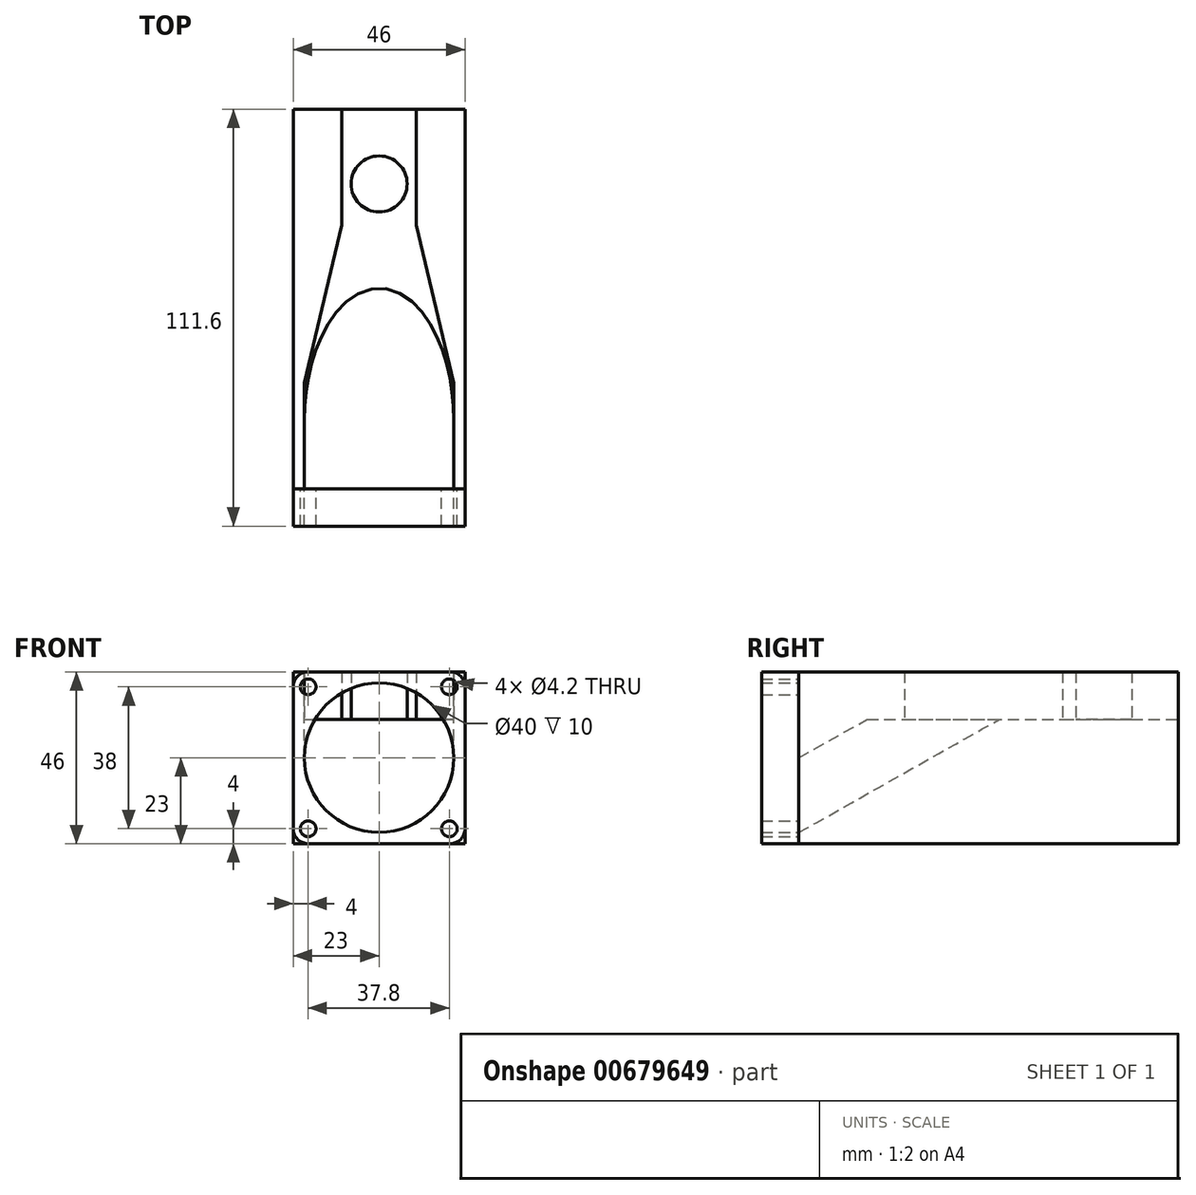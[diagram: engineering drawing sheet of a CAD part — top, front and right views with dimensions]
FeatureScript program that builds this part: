
annotation { "Feature Type Name" : "Feature", "Feature Type Description" : "" }
export const myFeature = defineFeature(function(context is Context, id is Id, definition is map)
    precondition{}
    {
        {
            var Q0;
            Q0=qCreatedBy(makeId("Front.planeOp"),FACE);
            var sketch = newSketch(context, id + "F0", { "sketchPlane" : qUnion([Q0])});
            skLineSegment(sketch, "E0.bottom", {"start": v(23, -23) * mm, "end": v(-23, -23) * mm});
            skLineSegment(sketch, "E0.top", {"start": v(23, 23) * mm, "end": v(-23, 23) * mm});
            skLineSegment(sketch, "E0.left", {"start": v(23, -23) * mm, "end": v(23, 23) * mm});
            skLineSegment(sketch, "E0.right", {"start": v(-23, -23) * mm, "end": v(-23, 23) * mm});
            skPoint(sketch, "E0.middle", {"position": v(0, 0) * mm});
            skSolve(sketch);
        }
        {
            var Q0;
            Q0=makeQuery(id+"F0.imprint","IMPRINT",FACE,{"disambiguationData":[TD([[makeQuery(id+"F0.imprint","IMPRINT",EDGE,{"derivedFrom":sQuery(id+"F0.wireOp",EDGE,"E0.bottom")}),-1.0]])]});
            extrude(context, id + "F1", {"entities" : qUnion([Q0]), "oppositeDirection" : true, "depth" : 101.6 * mm, "offsetDistance" : 25.4 * mm});
        }
        {
            var Q0;
            Q0=makeQuery(id+"F1.opExtrude","CAP_FACE",FACE,{"disambiguationData":[OSD([sQuery(id+"F0.wireOp",EDGE,"E0.bottom"),sQuery(id+"F0.wireOp",EDGE,"E0.top"),sQuery(id+"F0.wireOp",EDGE,"E0.left"),sQuery(id+"F0.wireOp",EDGE,"E0.right")])],"isStart":true});
            var sketch = newSketch(context, id + "F2", { "sketchPlane" : qUnion([Q0])});
            skArc(sketch, "E1", {"start": v(-20, 0) * mm, "mid": v(0, -20) * mm, "end": v(20, 0) * mm});
            skLineSegment(sketch, "E2.top", {"start": v(-20, 23) * mm, "end": v(20, 23) * mm});
            skLineSegment(sketch, "E2.left", {"start": v(-20, 0) * mm, "end": v(-20, 23) * mm});
            skLineSegment(sketch, "E2.right", {"start": v(20, 0) * mm, "end": v(20, 23) * mm});
            skSolve(sketch);
        }
        {
            var Q0;
            Q0=qCreatedBy(makeId("Right.planeOp"),FACE);
            var sketch = newSketch(context, id + "F3", { "sketchPlane" : qUnion([Q0])});
            skLineSegment(sketch, "E3", {"start": v(0, -20) * mm, "end": v(76.2, 23) * mm});
            skSolve(sketch);
        }
        {
            var Q0;
            Q0 = qSketchRegion(id + "F2", true);
            var Q1;
            Q1=sQuery(id+"F3.wireOp",EDGE,"E3");
            sweep(context, id + "F4", {"operationType" : NewBodyOperationType.REMOVE, "profiles" : qUnion([Q0]), "path" : qUnion([Q1])});
        }
        {
            var Q0;
            Q0=makeQuery(id+"F1.opExtrude","SWEPT_FACE",FACE,{"disambiguationData":[OSD([sQuery(id+"F0.wireOp",EDGE,"E0.top")])]});
            var sketch = newSketch(context, id + "F5", { "sketchPlane" : qUnion([Q0])});
            skLineSegment(sketch, "E4.bottom", {"start": v(-20, 0) * mm, "end": v(20, 0) * mm});
            skLineSegment(sketch, "E4.top", {"start": v(-20, 101.6) * mm, "end": v(20, 101.6) * mm});
            skLineSegment(sketch, "E4.left", {"start": v(-20, 0) * mm, "end": v(-20, 101.6) * mm});
            skLineSegment(sketch, "E4.right", {"start": v(20, 0) * mm, "end": v(20, 101.6) * mm});
            skSolve(sketch);
        }
        {
            var Q0;
            Q0 = qSketchRegion(id + "F5", true);
            extrude(context, id + "F6", {"entities" : qUnion([Q0]), "operationType" : NewBodyOperationType.REMOVE, "oppositeDirection" : true, "depth" : 12.7 * mm, "offsetDistance" : 25.4 * mm});
        }
        {
            var Q0;
            Q0=makeQuery(id+"F1.opExtrude","CAP_FACE",FACE,{"disambiguationData":[OSD([sQuery(id+"F0.wireOp",EDGE,"E0.bottom"),sQuery(id+"F0.wireOp",EDGE,"E0.top"),sQuery(id+"F0.wireOp",EDGE,"E0.left"),sQuery(id+"F0.wireOp",EDGE,"E0.right")])],"isStart":true});
            var sketch = newSketch(context, id + "F7", { "sketchPlane" : qUnion([Q0])});
            skCircle(sketch, "E5", {"center": v(0, 0) * mm, "radius": 20 * mm});
            skLineSegment(sketch, "E6.bottom", {"start": v(-23, -23) * mm, "end": v(23, -23) * mm});
            skLineSegment(sketch, "E6.top", {"start": v(-23, 23) * mm, "end": v(23, 23) * mm});
            skLineSegment(sketch, "E6.left", {"start": v(-23, -23) * mm, "end": v(-23, 23) * mm});
            skLineSegment(sketch, "E6.right", {"start": v(23, -23) * mm, "end": v(23, 23) * mm});
            skCircle(sketch, "E7", {"center": v(-19, 19) * mm, "radius": 2.1 * mm});
            skCircle(sketch, "E8", {"center": v(-19, -19) * mm, "radius": 2.1 * mm});
            skCircle(sketch, "E9", {"center": v(18.8, -19) * mm, "radius": 2.1 * mm});
            skCircle(sketch, "E10", {"center": v(18.8, 19) * mm, "radius": 2.1 * mm});
            skSolve(sketch);
        }
        {
            var Q0;
            Q0 = qSketchRegion(id + "F7", true);
            extrude(context, id + "F8", {"entities" : qUnion([Q0]), "depth" : 10 * mm, "offsetDistance" : 25.4 * mm});
        }
        {
            var Q0;
            Q0=makeQuery(id+"F8.opExtrude","SWEPT_EDGE",EDGE,{"disambiguationData":[OSD([sQuery(id+"F7.wireOp",EDGE,"E6.top"),sQuery(id+"F7.wireOp",EDGE,"E6.right")])]});
            var Q1;
            Q1=makeQuery(id+"F8.opExtrude","SWEPT_EDGE",EDGE,{"disambiguationData":[OSD([sQuery(id+"F7.wireOp",EDGE,"E6.top"),sQuery(id+"F7.wireOp",EDGE,"E6.left")])]});
            var Q2;
            Q2=makeQuery(id+"F8.opExtrude","SWEPT_EDGE",EDGE,{"disambiguationData":[OSD([sQuery(id+"F7.wireOp",EDGE,"E6.bottom"),sQuery(id+"F7.wireOp",EDGE,"E6.left")])]});
            var Q3;
            Q3=makeQuery(id+"F8.opExtrude","SWEPT_EDGE",EDGE,{"disambiguationData":[OSD([sQuery(id+"F7.wireOp",EDGE,"E6.bottom"),sQuery(id+"F7.wireOp",EDGE,"E6.right")])]});
            fillet(context, id + "F9", {"entities" : qUnion([Q0, Q1, Q2, Q3]), "radius" : 4 * mm, "tangentPropagation" : true, "allowEdgeOverflow" : false});
        }
        {
            var Q0;
            Q0=makeQuery(id+"F6.boolean.opBoolean","COPY",FACE,{"derivedFrom":makeQuery(id+"F6.opExtrude","CAP_FACE",FACE,{"disambiguationData":[OSD([sQuery(id+"F5.wireOp",EDGE,"E4.bottom"),sQuery(id+"F5.wireOp",EDGE,"E4.top"),sQuery(id+"F5.wireOp",EDGE,"E4.left"),sQuery(id+"F5.wireOp",EDGE,"E4.right")])],"isStart":false})});
            var sketch = newSketch(context, id + "F10", { "sketchPlane" : qUnion([Q0])});
            skCircle(sketch, "E11", {"center": v(0, 81.6) * mm, "radius": 7.5 * mm});
            skSolve(sketch);
        }
        {
            var Q0;
            Q0=makeQuery(id+"F10.imprint","IMPRINT",FACE,{"disambiguationData":[TD([[makeQuery(id+"F10.imprint","IMPRINT",EDGE,{"derivedFrom":sQuery(id+"F10.wireOp",EDGE,"E11")}),1.0]])]});
            extrude(context, id + "F11", {"entities" : qUnion([Q0]), "depth" : 12.7 * mm, "offsetDistance" : 25.4 * mm});
        }
        {
            var Q0;
            Q0=makeQuery(id+"F6.boolean.opBoolean","COPY",FACE,{"derivedFrom":makeQuery(id+"F6.opExtrude","CAP_FACE",FACE,{"disambiguationData":[OSD([sQuery(id+"F5.wireOp",EDGE,"E4.bottom"),sQuery(id+"F5.wireOp",EDGE,"E4.top"),sQuery(id+"F5.wireOp",EDGE,"E4.left"),sQuery(id+"F5.wireOp",EDGE,"E4.right")])],"isStart":false})});
            var sketch = newSketch(context, id + "F12", { "sketchPlane" : qUnion([Q0])});
            skLineSegment(sketch, "E12", {"start": v(-20, 28.32) * mm, "end": v(-10, 70.59) * mm});
            skLineSegment(sketch, "E13", {"start": v(-10, 70.59) * mm, "end": v(-10, 101.6) * mm});
            skLineSegment(sketch, "E14", {"start": v(-10, 101.6) * mm, "end": v(-20, 101.6) * mm});
            skLineSegment(sketch, "E15", {"start": v(-20, 101.6) * mm, "end": v(-20, 28.32) * mm});
            skLineSegment(sketch, "E16", {"start": v(20, 28.32) * mm, "end": v(10, 70.59) * mm});
            skLineSegment(sketch, "E17", {"start": v(10, 70.59) * mm, "end": v(10, 101.6) * mm});
            skLineSegment(sketch, "E18", {"start": v(10, 101.6) * mm, "end": v(20, 101.6) * mm});
            skLineSegment(sketch, "E19", {"start": v(20, 101.6) * mm, "end": v(20, 28.32) * mm});
            skSolve(sketch);
        }
        {
            var Q0;
            Q0=makeQuery(id+"F12.imprint","IMPRINT",FACE,{"disambiguationData":[TD([[makeQuery(id+"F12.imprint","IMPRINT",EDGE,{"derivedFrom":sQuery(id+"F12.wireOp",EDGE,"E12")}),1.0]])]});
            var Q1;
            Q1=makeQuery(id+"F12.imprint","IMPRINT",FACE,{"disambiguationData":[TD([[makeQuery(id+"F12.imprint","IMPRINT",EDGE,{"derivedFrom":sQuery(id+"F12.wireOp",EDGE,"E16")}),-1.0]])]});
            extrude(context, id + "F13", {"entities" : qUnion([Q0, Q1]), "operationType" : NewBodyOperationType.ADD, "depth" : 12.7 * mm, "offsetDistance" : 25.4 * mm});
        }
    });
